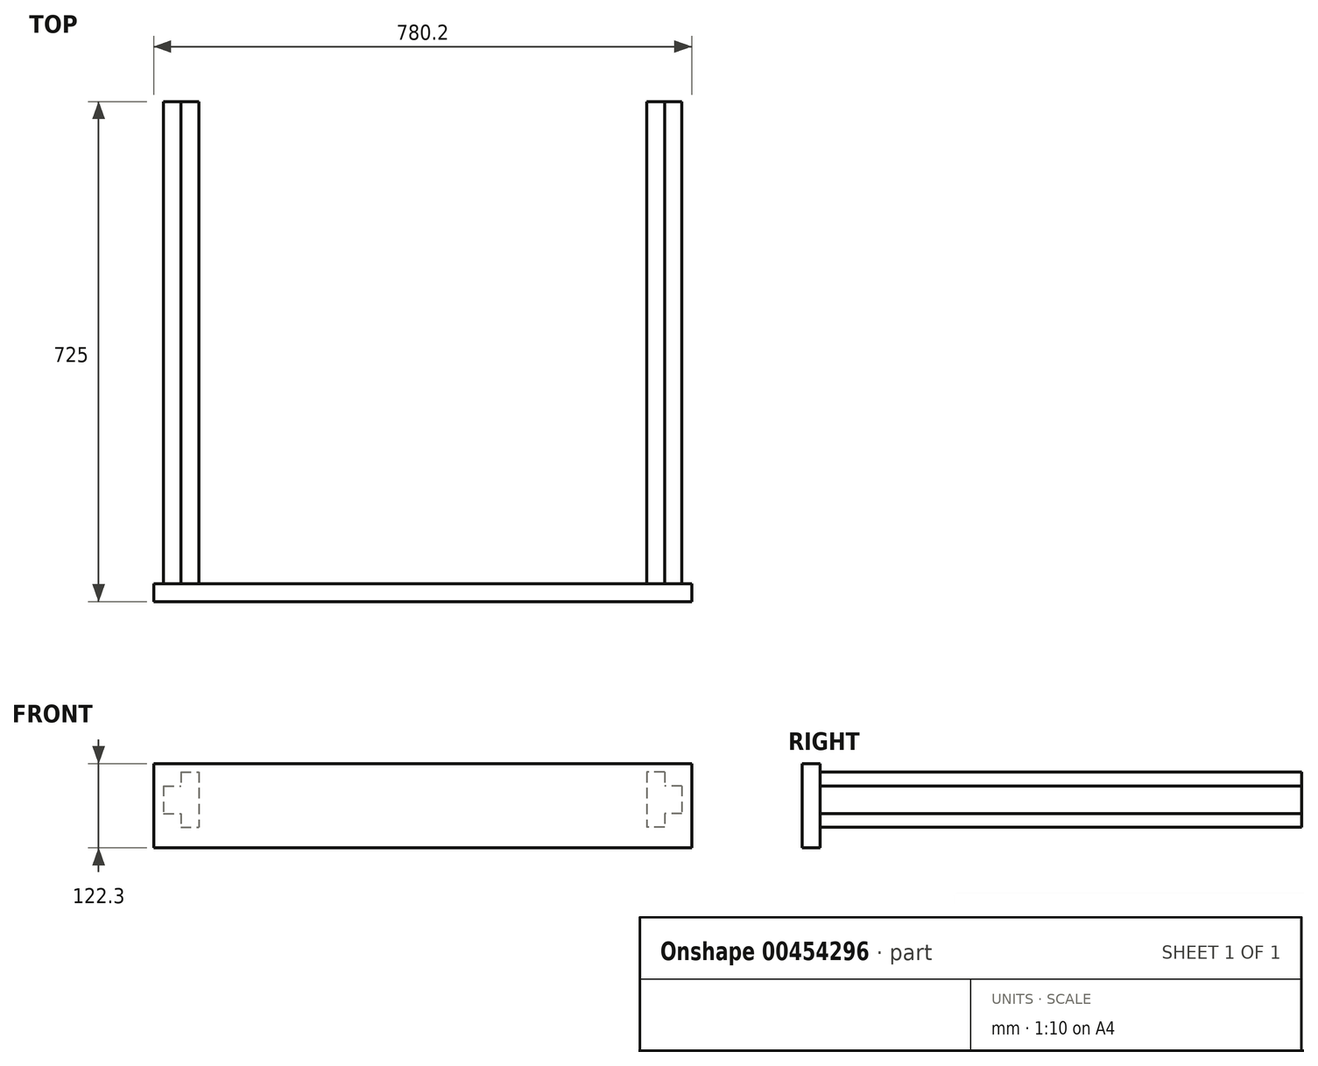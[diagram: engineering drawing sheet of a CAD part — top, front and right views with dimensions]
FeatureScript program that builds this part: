
annotation { "Feature Type Name" : "Feature", "Feature Type Description" : "" }
export const myFeature = defineFeature(function(context is Context, id is Id, definition is map)
    precondition{}
    {
        {
            var Q0;
            Q0=qCreatedBy(makeId("Front.planeOp"),FACE);
            var sketch = newSketch(context, id + "F0", { "sketchPlane" : qUnion([Q0])});
            skLineSegment(sketch, "E0.bottom", {"start": v(390.1, -61.15) * mm, "end": v(-390.1, -61.15) * mm});
            skLineSegment(sketch, "E0.top", {"start": v(390.1, 61.15) * mm, "end": v(-390.1, 61.15) * mm});
            skLineSegment(sketch, "E0.left", {"start": v(390.1, -61.15) * mm, "end": v(390.1, 61.15) * mm});
            skLineSegment(sketch, "E0.right", {"start": v(-390.1, -61.15) * mm, "end": v(-390.1, 61.15) * mm});
            skPoint(sketch, "E0.middle", {"position": v(0, 0) * mm});
            skSolve(sketch);
        }
        {
            var Q0;
            Q0=makeQuery(id+"F0.imprint","IMPRINT",FACE,{"disambiguationData":[TD([[makeQuery(id+"F0.imprint","IMPRINT",EDGE,{"derivedFrom":sQuery(id+"F0.wireOp",EDGE,"E0.bottom")}),-1.0]])]});
            extrude(context, id + "F1", {"entities" : qUnion([Q0]), "depth" : 26.1 * mm});
        }
        {
            var Q0;
            Q0=makeQuery(id+"F1.opExtrude","CAP_FACE",FACE,{"disambiguationData":[OSD([sQuery(id+"F0.wireOp",EDGE,"E0.bottom"),sQuery(id+"F0.wireOp",EDGE,"E0.top"),sQuery(id+"F0.wireOp",EDGE,"E0.left"),sQuery(id+"F0.wireOp",EDGE,"E0.right")])],"isStart":true});
            var sketch = newSketch(context, id + "F2", { "sketchPlane" : qUnion([Q0])});
            skPoint(sketch, "E1.middle", {"position": v(0, 0) * mm});
            skPoint(sketch, "E2", {"position": v(-350.95, 61.15) * mm});
            skPoint(sketch, "E3", {"position": v(-390.1, 61.15) * mm});
            skPoint(sketch, "E4", {"position": v(-390.1, 48.85) * mm});
            skPoint(sketch, "E5", {"position": v(-390.1, -61.15) * mm});
            skPoint(sketch, "E6", {"position": v(-390.1, -31.15) * mm});
            skPoint(sketch, "E7", {"position": v(-324.85, 61.15) * mm});
            skPoint(sketch, "E8", {"position": v(-375.95, 61.15) * mm});
            skPoint(sketch, "E9", {"position": v(-375.95, 28.85) * mm});
            skPoint(sketch, "E10", {"position": v(-375.95, 48.85) * mm});
            skLineSegment(sketch, "E11.bottom", {"start": v(-375.95, 28.85) * mm, "end": v(-350.95, 28.85) * mm});
            skLineSegment(sketch, "E11.top", {"start": v(-375.95, -11.15) * mm, "end": v(-350.95, -11.15) * mm});
            skLineSegment(sketch, "E11.left", {"start": v(-375.95, 28.85) * mm, "end": v(-375.95, -11.15) * mm});
            skLineSegment(sketch, "E11.right", {"start": v(-350.95, 28.85) * mm, "end": v(-350.95, -11.15) * mm});
            skLineSegment(sketch, "E12.bottom", {"start": v(-350.95, 48.85) * mm, "end": v(-324.85, 48.85) * mm});
            skLineSegment(sketch, "E12.top", {"start": v(-350.95, -31.15) * mm, "end": v(-324.85, -31.15) * mm});
            skLineSegment(sketch, "E12.left", {"start": v(-350.95, 48.85) * mm, "end": v(-350.95, -31.15) * mm});
            skLineSegment(sketch, "E12.right", {"start": v(-324.85, 48.85) * mm, "end": v(-324.85, -31.15) * mm});
            skPoint(sketch, "E13.startSnap0", {"position": v(0, 48.85) * mm});
            skLineSegment(sketch, "E14", {"start": v(0, 84.46) * mm, "end": v(0, -104.89) * mm, "construction": true});
            skPoint(sketch, "E14.startSnap0", {"position": v(0, 61.15) * mm});
            skLineSegment(sketch, "E15.MirrorCS", {"start": v(350.95, 48.85) * mm, "end": v(324.85, 48.85) * mm});
            skLineSegment(sketch, "E16.MirrorCS", {"start": v(324.85, 48.85) * mm, "end": v(324.85, -31.15) * mm});
            skLineSegment(sketch, "E17.MirrorCS", {"start": v(350.95, 48.85) * mm, "end": v(350.95, -31.15) * mm});
            skLineSegment(sketch, "E18.MirrorCS", {"start": v(375.95, 28.85) * mm, "end": v(350.95, 28.85) * mm});
            skLineSegment(sketch, "E19.MirrorCS", {"start": v(375.95, 28.85) * mm, "end": v(375.95, -11.15) * mm});
            skLineSegment(sketch, "E20.MirrorCS", {"start": v(375.95, -11.15) * mm, "end": v(350.95, -11.15) * mm});
            skLineSegment(sketch, "E21.MirrorCS", {"start": v(350.95, -31.15) * mm, "end": v(324.85, -31.15) * mm});
            skPoint(sketch, "E22", {"position": v(350.95, -61.15) * mm});
            skPoint(sketch, "E23", {"position": v(390.1, -11.15) * mm});
            skSolve(sketch);
        }
        {
            var Q0;
            {var subQ3=sQuery(id+"F2.wireOp",EDGE,"E12.bottom");Q0=makeQuery(id+"F2.imprint","IMPRINT",FACE,{"disambiguationData":[TD([[makeQuery(id+"F2.imprint","IMPRINT",EDGE,{"derivedFrom":subQ3}),-1.0]])]});}
            var Q1;
            {var subQ3=sQuery(id+"F2.wireOp",EDGE,"E15.MirrorCS");Q1=makeQuery(id+"F2.imprint","IMPRINT",FACE,{"disambiguationData":[TD([[makeQuery(id+"F2.imprint","IMPRINT",EDGE,{"derivedFrom":subQ3}),1.0]])]});}
            var Q2;
            {var subQ0=sQuery(id+"F2.wireOp",EDGE,"E18.MirrorCS");Q2=makeQuery(id+"F2.imprint","IMPRINT",FACE,{"disambiguationData":[TD([[makeQuery(id+"F2.imprint","IMPRINT",EDGE,{"derivedFrom":subQ0}),1.0]])]});}
            var Q3;
            {var subQ0=sQuery(id+"F2.wireOp",EDGE,"E11.bottom");Q3=makeQuery(id+"F2.imprint","IMPRINT",FACE,{"disambiguationData":[TD([[makeQuery(id+"F2.imprint","IMPRINT",EDGE,{"derivedFrom":subQ0}),-1.0]])]});}
            extrude(context, id + "F3", {"entities" : qUnion([Q0, Q1, Q2, Q3]), "operationType" : NewBodyOperationType.ADD, "depth" : 698.9 * mm});
        }
    });
